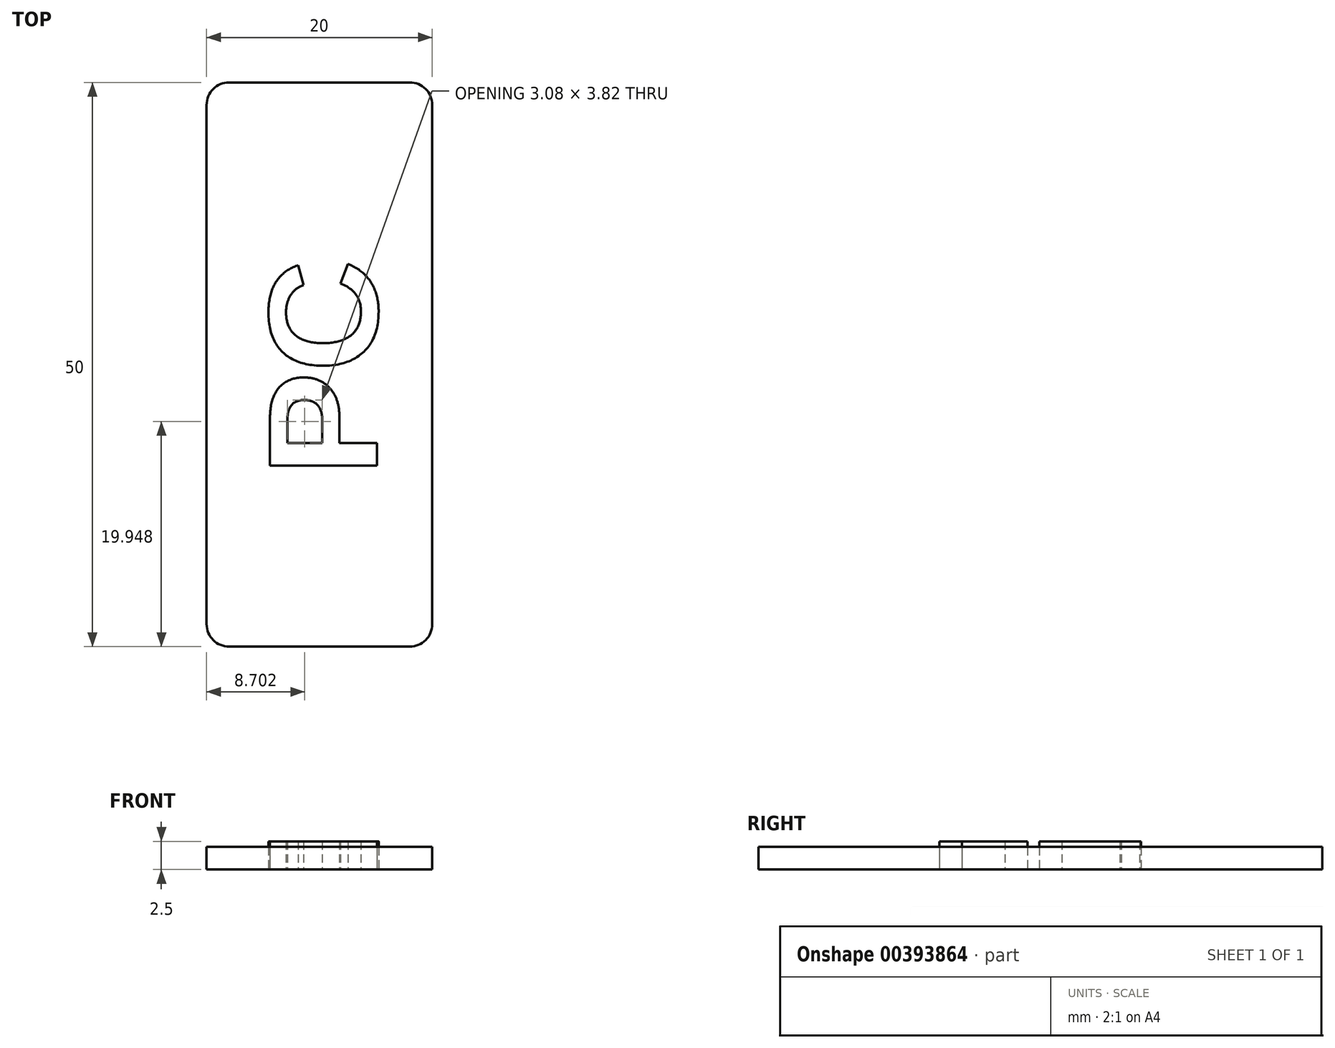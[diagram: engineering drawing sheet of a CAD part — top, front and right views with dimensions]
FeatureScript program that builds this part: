
annotation { "Feature Type Name" : "Feature", "Feature Type Description" : "" }
export const myFeature = defineFeature(function(context is Context, id is Id, definition is map)
    precondition{}
    {
        {
            var Q0;
            Q0=qCreatedBy(makeId("Top.planeOp"),FACE);
            var sketch = newSketch(context, id + "F0", { "sketchPlane" : qUnion([Q0])});
            skLineSegment(sketch, "E0.bottom", {"start": v(-20, -25) * mm, "end": v(0, -25) * mm});
            skLineSegment(sketch, "E0.top", {"start": v(-20, 25) * mm, "end": v(0, 25) * mm});
            skLineSegment(sketch, "E0.left", {"start": v(-20, -25) * mm, "end": v(-20, 25) * mm});
            skLineSegment(sketch, "E0.right", {"start": v(0, -25) * mm, "end": v(0, 25) * mm});
            skSolve(sketch);
        }
        {
            var Q0;
            Q0=makeQuery(id+"F0.imprint","IMPRINT",FACE,{"disambiguationData":[TD([[makeQuery(id+"F0.imprint","IMPRINT",EDGE,{"derivedFrom":sQuery(id+"F0.wireOp",EDGE,"E0.bottom")}),1.0]])]});
            extrude(context, id + "F1", {"entities" : qUnion([Q0]), "depth" : 2 * mm});
        }
        {
            var Q0;
            Q0=makeQuery(id+"F1.opExtrude","SWEPT_EDGE",EDGE,{"disambiguationData":[OSD([sQuery(id+"F0.wireOp",EDGE,"E0.bottom"),sQuery(id+"F0.wireOp",EDGE,"E0.right")])]});
            var Q1;
            Q1=makeQuery(id+"F1.opExtrude","SWEPT_EDGE",EDGE,{"disambiguationData":[OSD([sQuery(id+"F0.wireOp",EDGE,"E0.bottom"),sQuery(id+"F0.wireOp",EDGE,"E0.left")])]});
            var Q2;
            Q2=makeQuery(id+"F1.opExtrude","SWEPT_EDGE",EDGE,{"disambiguationData":[OSD([sQuery(id+"F0.wireOp",EDGE,"E0.top"),sQuery(id+"F0.wireOp",EDGE,"E0.right")])]});
            var Q3;
            Q3=makeQuery(id+"F1.opExtrude","SWEPT_EDGE",EDGE,{"disambiguationData":[OSD([sQuery(id+"F0.wireOp",EDGE,"E0.top"),sQuery(id+"F0.wireOp",EDGE,"E0.left")])]});
            fillet(context, id + "F2", {"entities" : qUnion([Q0, Q1, Q2, Q3]), "radius" : 2 * mm, "tangentPropagation" : true, "allowEdgeOverflow" : false});
        }
        {
            var Q0;
            Q0=qCreatedBy(makeId("Top.planeOp"),FACE);
            var sketch = newSketch(context, id + "F3", { "sketchPlane" : qUnion([Q0])});
            skText(sketch, "E1", { "text": "PC", "fontName": "Arimo-Bold.ttf"});
            const initialGuessF3  = {"E1": [-0.00489, -0.00987, 0, 1, 0.00993]};
            skSetInitialGuess(sketch, initialGuessF3);
            skSolve(sketch);
        }
        {
            var Q0;
            Q0=qSketchRegion(id+"F3",true);
            extrude(context, id + "F4", {"entities" : qUnion([Q0]), "depth" : 2.5 * mm});
        }
    });
